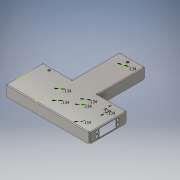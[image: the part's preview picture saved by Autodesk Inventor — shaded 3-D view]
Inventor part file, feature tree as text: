
AUTODESK INVENTOR PART (.ipt)
format: ipt  version: 2016 (Build 200138000, 138)  size: 374,272 bytes
history: native  units: in
note: dims shown in document units (in); Inventor stores cm internally (conversion verified against a paired STEP export)
features: sketch x13, other x11, sheet_metal_op x6, fillet x3
ambient origin geometry x8: Origin, YZ Plane, XZ Plane, XY Plane, X Axis, Y Axis, Z Axis, Center Point
bodies: Solid1 (feature_tree)
feature tree (33):
  sheet_metal_op  "Face1"
  sheet_metal_op  "Face2"
  sheet_metal_op  "Flange1"
  sketch  "Sketch9"  dims[d12=3.4374in]
  sketch  "Sketch18"  dims[d14=0.034in]
  sketch  "Sketch21"  dims[d16=0.068in]
  sketch  "Sketch22"  dims[d17=0.034in]
  fillet  "Fillet1"  Radius=2.3in
  fillet  "Fillet2"  Radius=8.0in
  fillet  "Fillet3"  Radius=0.034in
  sketch  "Sketch24"  dims[d19=0.017in]
  sketch  "Sketch25"  dims[d20=0.068in]
  sketch  "Sketch26"  dims[d21=0.034in d22=1.0in d23=90.0deg d24=0.034in d25=0.136in d26=0.034in d27=0.034in d40=0.034in d41=0.0in d42=0.8in d53=0.917in d55=0.034in d56=0.0in d57=0.917in d64=45.0deg d65=0.034in d66=0.0in d67=0.917in d71=1.625in d72=12.0in d73=0.0in d74=12.0in d75=0.0in d76=0.034in d77=0.0in d78=0.034in d79=0.0in d81=0.034in d82=0.0in d83=0.125in d84=0.125in d85=0.125in d86=0.231in d87=0.25in d92=0.134in d93=0.134in d94=0.134in d96=0.134in d99=0.134in d100=0.134in d101=0.134in d102=0.134in]
  sketch  "Sketch2"  dims[d9=3.4374in]
  other  "Plate1"
  sketch  "Sketch4"  dims[d10=2.7993in]
  other  "Plate2"
  sheet_metal_op  "Bend1"
  sketch  "Sketch5"  dims[d11=2.799in]
  other  "Plate3"
  sheet_metal_op  "Bend2"
  sheet_metal_op  "Corner1"
  sketch  "Sketch13"  dims[d13=0.034in]
  sketch  "Sketch20"  dims[d15=0.017in]
  sketch  "Sketch23"  dims[d18=0.034in]
  other  "Cut5"
  other  "Cut7"
  other  "Cut10"
  other  "Cut12"
  other  "Cut13"
  other  "Cut14"
  other  "Cut15"
  other  "Cut16"
